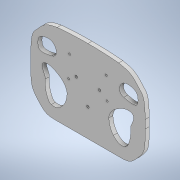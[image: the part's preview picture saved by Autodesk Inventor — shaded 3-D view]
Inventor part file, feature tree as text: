
AUTODESK INVENTOR PART (.ipt)
format: ipt  version: 2021 (Build 250183000, 183)  size: 217,600 bytes
history: native  units: in
note: dims shown in document units (in); Inventor stores cm internally (conversion verified against a paired STEP export)
features: extrude x1, mirror x1, sketch x1
ambient origin geometry x8: Origin, YZ Plane, XZ Plane, XY Plane, X Axis, Y Axis, Z Axis, Center Point
bodies: Solid1 (feature_tree), Solid2 (feature_tree)
feature tree (3):
  extrude  "Extrusion1"  [1 undecoded]
  mirror  "Mirror1"
  sketch  "Sketch1"  dims[d0=1.0in d1=0.0in]
note: 1 required parameter value undecoded (feature->parameter linkage not recoverable at this tier; creation-order binding heuristic only, values carry confidence <= 0.55)
